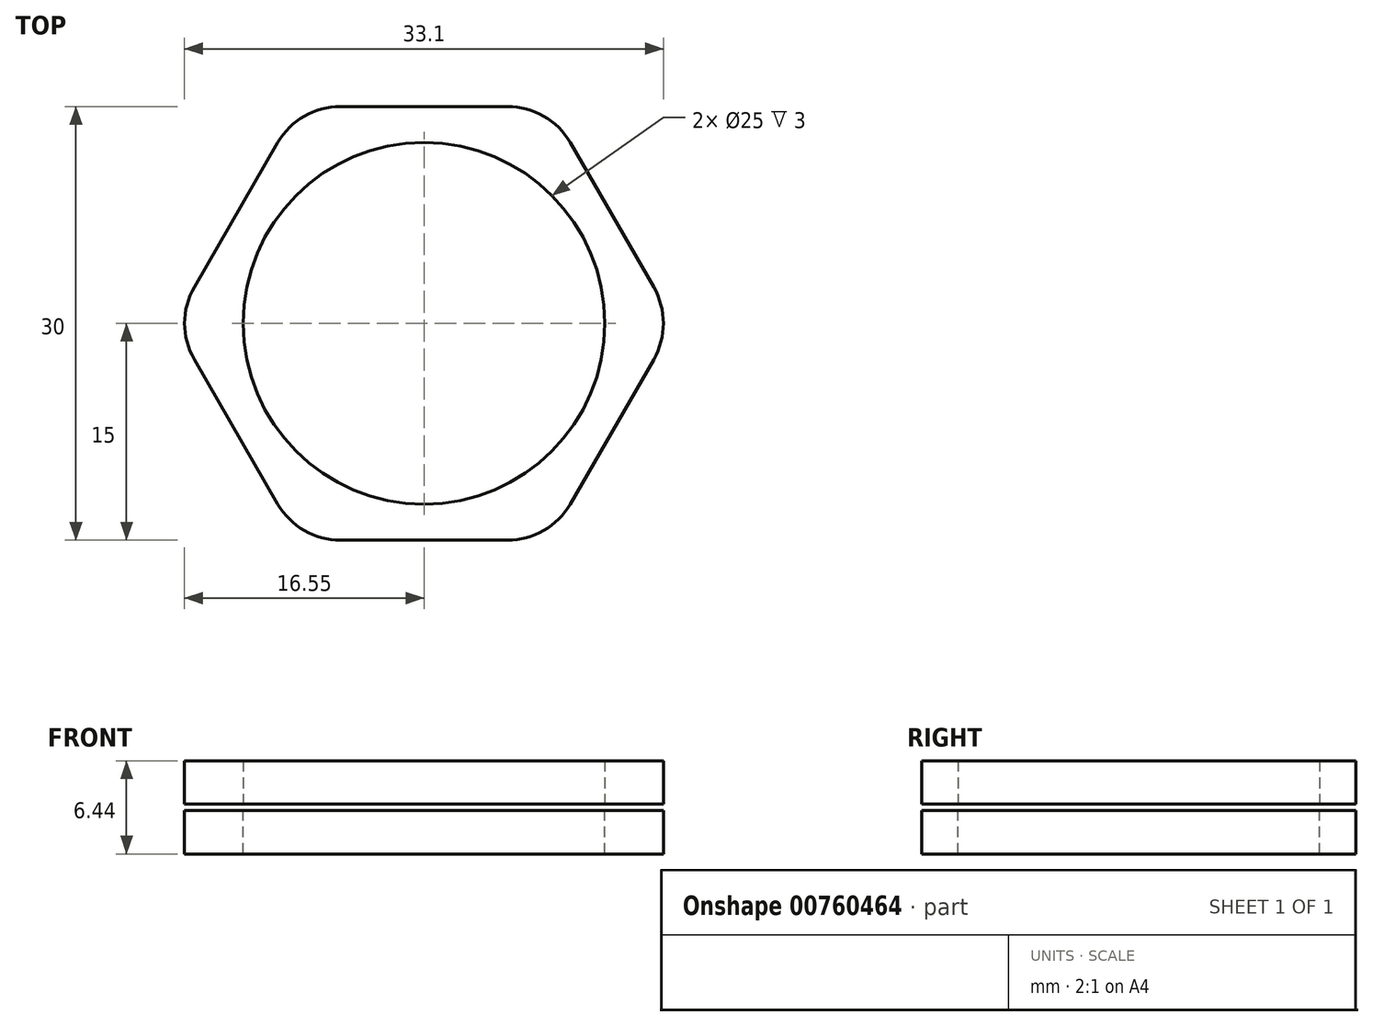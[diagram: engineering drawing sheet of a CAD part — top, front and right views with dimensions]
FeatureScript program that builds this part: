
annotation { "Feature Type Name" : "Feature", "Feature Type Description" : "" }
export const myFeature = defineFeature(function(context is Context, id is Id, definition is map)
    precondition{}
    {
        {
            var Q0;
            Q0=qCreatedBy(makeId("Top.planeOp"),FACE);
            var sketch = newSketch(context, id + "F0", { "sketchPlane" : qUnion([Q0])});
            skCircle(sketch, "E0.cCircle", {"center": v(0, 0) * mm, "radius": 15 * mm, "construction": true});
            skLineSegment(sketch, "E0.0", {"start": v(-8.66, 15) * mm, "end": v(8.66, 15) * mm});
            skLineSegment(sketch, "E0.1", {"start": v(8.66, 15) * mm, "end": v(17.32, 0) * mm});
            skLineSegment(sketch, "E0.2", {"start": v(17.32, 0) * mm, "end": v(8.66, -15) * mm});
            skLineSegment(sketch, "E0.3", {"start": v(8.66, -15) * mm, "end": v(-8.66, -15) * mm});
            skLineSegment(sketch, "E0.4", {"start": v(-8.66, -15) * mm, "end": v(-17.32, 0) * mm});
            skLineSegment(sketch, "E0.5", {"start": v(-17.32, 0) * mm, "end": v(-8.66, 15) * mm});
            skPoint(sketch, "E0.0.midPoint", {"position": v(0, 15) * mm});
            skCircle(sketch, "E1", {"center": v(0, 0) * mm, "radius": 12.5 * mm});
            skSolve(sketch);
        }
        {
            var Q0;
            Q0=makeQuery(id+"F0.imprint","IMPRINT",FACE,{"disambiguationData":[TD([[makeQuery(id+"F0.imprint","IMPRINT",EDGE,{"derivedFrom":sQuery(id+"F0.wireOp",EDGE,"E0.0")}),-1.0]])]});
            extrude(context, id + "F1", {"entities" : qUnion([Q0]), "depth" : 3 * mm, "offsetDistance" : 25 * mm});
        }
        {
            var Q0;
            Q0=makeQuery(id+"F1.opExtrude","SWEPT_EDGE",EDGE,{"disambiguationData":[OSD([sQuery(id+"F0.wireOp",EDGE,"E0.4"),sQuery(id+"F0.wireOp",EDGE,"E0.5")])]});
            var Q1;
            Q1=makeQuery(id+"F1.opExtrude","SWEPT_EDGE",EDGE,{"disambiguationData":[OSD([sQuery(id+"F0.wireOp",EDGE,"E0.3"),sQuery(id+"F0.wireOp",EDGE,"E0.4")])]});
            var Q2;
            Q2=makeQuery(id+"F1.opExtrude","SWEPT_EDGE",EDGE,{"disambiguationData":[OSD([sQuery(id+"F0.wireOp",EDGE,"E0.2"),sQuery(id+"F0.wireOp",EDGE,"E0.3")])]});
            var Q3;
            Q3=makeQuery(id+"F1.opExtrude","SWEPT_EDGE",EDGE,{"disambiguationData":[OSD([sQuery(id+"F0.wireOp",EDGE,"E0.1"),sQuery(id+"F0.wireOp",EDGE,"E0.2")])]});
            var Q4;
            Q4=makeQuery(id+"F1.opExtrude","SWEPT_EDGE",EDGE,{"disambiguationData":[OSD([sQuery(id+"F0.wireOp",EDGE,"E0.0"),sQuery(id+"F0.wireOp",EDGE,"E0.1")])]});
            var Q5;
            Q5=makeQuery(id+"F1.opExtrude","SWEPT_EDGE",EDGE,{"disambiguationData":[OSD([sQuery(id+"F0.wireOp",EDGE,"E0.0"),sQuery(id+"F0.wireOp",EDGE,"E0.5")])]});
            fillet(context, id + "F2", {"entities" : qUnion([Q0, Q1, Q2, Q3, Q4, Q5]), "radius" : 5 * mm, "tangentPropagation" : true, "allowEdgeOverflow" : false});
        }
        {
            var Q0;
            Q0=makeQuery(id+"F1.opExtrude","SWEPT_BODY",BODY,{"disambiguationData":[OSD([sQuery(id+"F0.wireOp",EDGE,"E0.0"),sQuery(id+"F0.wireOp",EDGE,"E0.1"),sQuery(id+"F0.wireOp",EDGE,"E0.2"),sQuery(id+"F0.wireOp",EDGE,"E0.3"),sQuery(id+"F0.wireOp",EDGE,"E0.4"),sQuery(id+"F0.wireOp",EDGE,"E0.5"),sQuery(id+"F0.wireOp",EDGE,"E1")])]});
            transform(context, id + "F3", {"entities" : qUnion([Q0]), "transformType" : TransformType.TRANSLATION_3D, "dx" : 0 * mm, "dy" : 0 * mm, "dz" : 0.22 * mm, "makeCopy" : false});
        }
        {
            var Q0;
            Q0=makeQuery(id+"F1.opExtrude","SWEPT_BODY",BODY,{"disambiguationData":[OSD([sQuery(id+"F0.wireOp",EDGE,"E0.0"),sQuery(id+"F0.wireOp",EDGE,"E0.1"),sQuery(id+"F0.wireOp",EDGE,"E0.2"),sQuery(id+"F0.wireOp",EDGE,"E0.3"),sQuery(id+"F0.wireOp",EDGE,"E0.4"),sQuery(id+"F0.wireOp",EDGE,"E0.5"),sQuery(id+"F0.wireOp",EDGE,"E1")])]});
            var Q1;
            Q1=qCreatedBy(makeId("Top.planeOp"),FACE);
            mirror(context, id + "F4", {"entities" : qUnion([Q0]), "mirrorPlane" : qUnion([Q1])});
        }
    });
